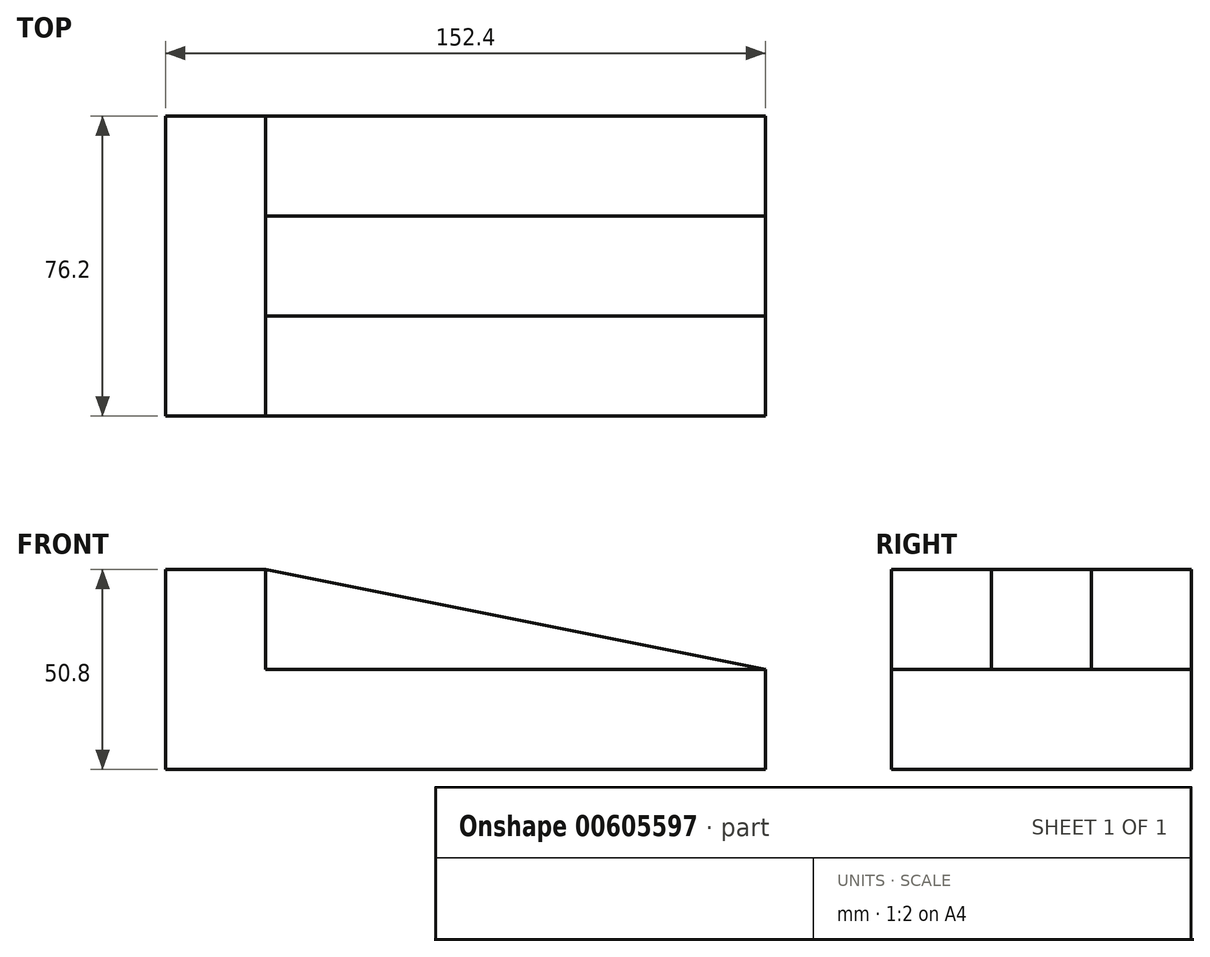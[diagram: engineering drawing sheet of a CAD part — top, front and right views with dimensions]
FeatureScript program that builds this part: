
annotation { "Feature Type Name" : "Feature", "Feature Type Description" : "" }
export const myFeature = defineFeature(function(context is Context, id is Id, definition is map)
    precondition{}
    {
        {
            var Q0;
            Q0=qCreatedBy(makeId("Front.planeOp"),FACE);
            var sketch = newSketch(context, id + "F0", { "sketchPlane" : qUnion([Q0])});
            skLineSegment(sketch, "E0", {"start": v(-152.4, 0) * mm, "end": v(-152.4, 50.8) * mm});
            skLineSegment(sketch, "E1", {"start": v(-152.4, 50.8) * mm, "end": v(0, 50.8) * mm});
            skLineSegment(sketch, "E2", {"start": v(0, 50.8) * mm, "end": v(0, 0) * mm});
            skLineSegment(sketch, "E3", {"start": v(-152.4, 0) * mm, "end": v(0, 0) * mm});
            skSolve(sketch);
        }
        {
            var Q0;
            Q0=makeQuery(id+"F0.imprint","IMPRINT",FACE,{"disambiguationData":[TD([[makeQuery(id+"F0.imprint","IMPRINT",EDGE,{"derivedFrom":sQuery(id+"F0.wireOp",EDGE,"E0")}),-1.0]])]});
            extrude(context, id + "F1", {"entities" : qUnion([Q0]), "depth" : 76.2 * mm, "offsetDistance" : 25.4 * mm});
        }
        {
            var Q0;
            Q0=makeQuery(id+"F1.opExtrude","SWEPT_FACE",FACE,{"disambiguationData":[OSD([sQuery(id+"F0.wireOp",EDGE,"E1")])]});
            var sketch = newSketch(context, id + "F2", { "sketchPlane" : qUnion([Q0])});
            skLineSegment(sketch, "E4.bottom", {"start": v(0, -76.2) * mm, "end": v(-127, -76.2) * mm});
            skLineSegment(sketch, "E4.top", {"start": v(0, -50.8) * mm, "end": v(-127, -50.8) * mm});
            skLineSegment(sketch, "E4.left", {"start": v(0, -76.2) * mm, "end": v(0, -50.8) * mm});
            skLineSegment(sketch, "E4.right", {"start": v(-127, -76.2) * mm, "end": v(-127, -50.8) * mm});
            skLineSegment(sketch, "E5.bottom", {"start": v(0, 0) * mm, "end": v(-127, 0) * mm});
            skLineSegment(sketch, "E5.top", {"start": v(0, -25.4) * mm, "end": v(-127, -25.4) * mm});
            skLineSegment(sketch, "E5.left", {"start": v(0, 0) * mm, "end": v(0, -25.4) * mm});
            skLineSegment(sketch, "E5.right", {"start": v(-127, 0) * mm, "end": v(-127, -25.4) * mm});
            skSolve(sketch);
        }
        {
            var Q0;
            Q0=makeQuery(id+"F2.imprint","IMPRINT",FACE,{"disambiguationData":[TD([[makeQuery(id+"F2.imprint","IMPRINT",EDGE,{"derivedFrom":sQuery(id+"F2.wireOp",EDGE,"E5.bottom")}),-1.0]])]});
            var Q1;
            Q1=makeQuery(id+"F2.imprint","IMPRINT",FACE,{"disambiguationData":[TD([[makeQuery(id+"F2.imprint","IMPRINT",EDGE,{"derivedFrom":sQuery(id+"F2.wireOp",EDGE,"E4.bottom")}),1.0]])]});
            extrude(context, id + "F3", {"entities" : qUnion([Q0, Q1]), "operationType" : NewBodyOperationType.REMOVE, "oppositeDirection" : true, "depth" : 25.4 * mm, "offsetDistance" : 25.4 * mm});
        }
        {
            var Q0;
            Q0=makeQuery(id+"F3.boolean.opBoolean","COPY",FACE,{"derivedFrom":makeQuery(id+"F3.opExtrude","SWEPT_FACE",FACE,{"disambiguationData":[OSD([sQuery(id+"F2.wireOp",EDGE,"E4.top")])]})});
            var sketch = newSketch(context, id + "F4", { "sketchPlane" : qUnion([Q0])});
            skLineSegment(sketch, "E6", {"start": v(-127, 50.8) * mm, "end": v(0, 25.4) * mm});
            skLineSegment(sketch, "E7", {"start": v(0, 25.4) * mm, "end": v(0, 50.8) * mm});
            skLineSegment(sketch, "E8", {"start": v(0, 50.8) * mm, "end": v(-127, 50.8) * mm});
            skSolve(sketch);
        }
        {
            var Q0;
            Q0=makeQuery(id+"F4.imprint","IMPRINT",FACE,{"disambiguationData":[TD([[makeQuery(id+"F4.imprint","IMPRINT",EDGE,{"derivedFrom":sQuery(id+"F4.wireOp",EDGE,"E6")}),1.0]])]});
            extrude(context, id + "F5", {"entities" : qUnion([Q0]), "operationType" : NewBodyOperationType.REMOVE, "oppositeDirection" : true, "depth" : 25.4 * mm, "offsetDistance" : 25.4 * mm});
        }
    });
